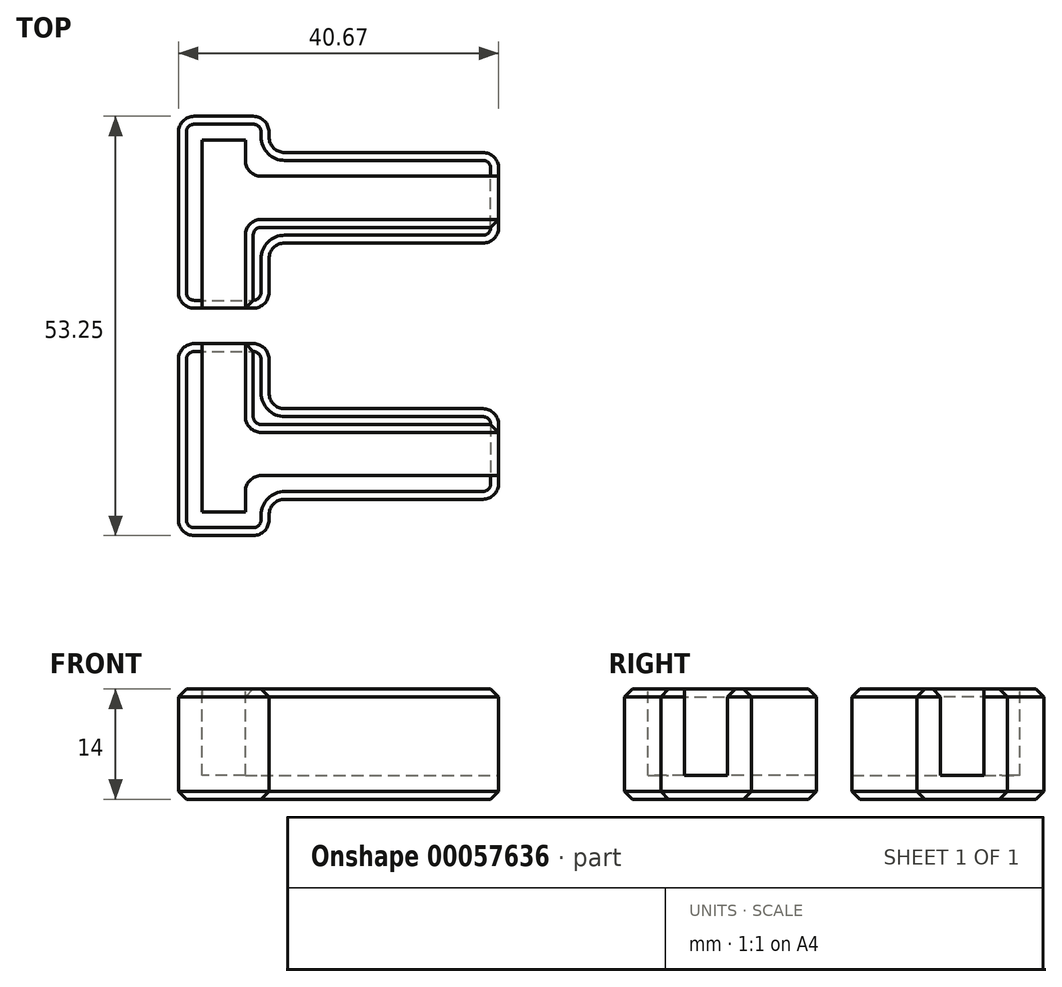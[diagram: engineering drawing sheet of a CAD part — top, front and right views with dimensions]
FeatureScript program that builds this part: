
annotation { "Feature Type Name" : "Feature", "Feature Type Description" : "" }
export const myFeature = defineFeature(function(context is Context, id is Id, definition is map)
    precondition{}
    {
        {
            var Q0;
            Q0=qCreatedBy(makeId("Top.planeOp"),FACE);
            var sketch = newSketch(context, id + "F0", { "sketchPlane" : qUnion([Q0])});
            skLineSegment(sketch, "E0", {"start": v(-6.24, -15.63) * mm, "end": v(22.93, -15.63) * mm});
            skLineSegment(sketch, "E1", {"start": v(22.93, -15.63) * mm, "end": v(22.93, -4.13) * mm});
            skLineSegment(sketch, "E2", {"start": v(22.93, -4.13) * mm, "end": v(-6.24, -4.13) * mm});
            skLineSegment(sketch, "E3", {"start": v(-6.24, -4.13) * mm, "end": v(-6.24, 4.14) * mm});
            skLineSegment(sketch, "E4", {"start": v(-6.24, 4.14) * mm, "end": v(-17.74, 4.14) * mm});
            skLineSegment(sketch, "E5", {"start": v(-17.74, 4.14) * mm, "end": v(-17.74, -20.23) * mm});
            skLineSegment(sketch, "E6", {"start": v(-17.74, -20.23) * mm, "end": v(-6.24, -20.23) * mm});
            skLineSegment(sketch, "E7", {"start": v(-6.24, -20.23) * mm, "end": v(-6.24, -15.63) * mm});
            skLineSegment(sketch, "E8", {"start": v(-14.74, 4.14) * mm, "end": v(-14.74, -17.23) * mm});
            skLineSegment(sketch, "E9", {"start": v(-14.74, -17.23) * mm, "end": v(-9.24, -17.23) * mm});
            skLineSegment(sketch, "E10", {"start": v(-9.24, -17.23) * mm, "end": v(-9.24, -12.63) * mm});
            skLineSegment(sketch, "E11", {"start": v(-9.24, -12.63) * mm, "end": v(22.93, -12.63) * mm});
            skLineSegment(sketch, "E12", {"start": v(-9.24, 4.14) * mm, "end": v(-9.24, -7.13) * mm});
            skLineSegment(sketch, "E13", {"start": v(-9.24, -7.13) * mm, "end": v(22.93, -7.13) * mm});
            skSolve(sketch);
        }
        {
            var Q0;
            Q0 = qSketchRegion(id + "F0", true);
            extrude(context, id + "F1", {"entities" : qUnion([Q0]), "oppositeDirection" : true, "depth" : 14 * mm});
        }
        {
            var Q0;
            {var subQ1=sQuery(id+"F0.wireOp",EDGE,"E8");Q0=makeQuery(id+"F0.imprint","IMPRINT",FACE,{"disambiguationData":[TD([[makeQuery(id+"F0.imprint","IMPRINT",EDGE,{"derivedFrom":subQ1}),1.0]])]});}
            extrude(context, id + "F2", {"entities" : qUnion([Q0]), "operationType" : NewBodyOperationType.REMOVE, "oppositeDirection" : true, "depth" : 11 * mm});
        }
        {
            var Q0;
            Q0=makeQuery(id+"F1.opExtrude","SWEPT_EDGE",EDGE,{"disambiguationData":[OSD([sQuery(id+"F0.wireOp",EDGE,"E6"),sQuery(id+"F0.wireOp",EDGE,"E7")])]});
            var Q1;
            Q1=makeQuery(id+"F1.opExtrude","SWEPT_EDGE",EDGE,{"disambiguationData":[OSD([sQuery(id+"F0.wireOp",EDGE,"E5"),sQuery(id+"F0.wireOp",EDGE,"E6")])]});
            var Q2;
            Q2=makeQuery(id+"F1.opExtrude","SWEPT_EDGE",EDGE,{"disambiguationData":[OSD([sQuery(id+"F0.wireOp",EDGE,"E0"),sQuery(id+"F0.wireOp",EDGE,"E7")])]});
            var Q3;
            Q3=makeQuery(id+"F1.opExtrude","SWEPT_EDGE",EDGE,{"disambiguationData":[OSD([sQuery(id+"F0.wireOp",EDGE,"E0"),sQuery(id+"F0.wireOp",EDGE,"E1")])]});
            var Q4;
            Q4=makeQuery(id+"F1.opExtrude","SWEPT_EDGE",EDGE,{"disambiguationData":[OSD([sQuery(id+"F0.wireOp",EDGE,"E4"),sQuery(id+"F0.wireOp",EDGE,"E5")])]});
            var Q5;
            Q5=makeQuery(id+"F1.opExtrude","SWEPT_EDGE",EDGE,{"disambiguationData":[OSD([sQuery(id+"F0.wireOp",EDGE,"E3"),sQuery(id+"F0.wireOp",EDGE,"E4")])]});
            var Q6;
            Q6=makeQuery(id+"F1.opExtrude","SWEPT_EDGE",EDGE,{"disambiguationData":[OSD([sQuery(id+"F0.wireOp",EDGE,"E1"),sQuery(id+"F0.wireOp",EDGE,"E2")])]});
            var Q7;
            Q7=makeQuery(id+"F1.opExtrude","SWEPT_EDGE",EDGE,{"disambiguationData":[OSD([sQuery(id+"F0.wireOp",EDGE,"E2"),sQuery(id+"F0.wireOp",EDGE,"E3")])]});
            var Q8;
            Q8=makeQuery(id+"F2.boolean.opBoolean","COPY",EDGE,{"derivedFrom":makeQuery(id+"F2.opExtrude","SWEPT_EDGE",EDGE,{"disambiguationData":[OSD([sQuery(id+"F0.wireOp",EDGE,"E10"),sQuery(id+"F0.wireOp",EDGE,"E11")])]})});
            var Q9;
            Q9=makeQuery(id+"F2.boolean.opBoolean","COPY",EDGE,{"derivedFrom":makeQuery(id+"F2.opExtrude","SWEPT_EDGE",EDGE,{"disambiguationData":[OSD([sQuery(id+"F0.wireOp",EDGE,"E12"),sQuery(id+"F0.wireOp",EDGE,"E13")])]})});
            fillet(context, id + "F3", {"entities" : qUnion([Q0, Q1, Q2, Q3, Q4, Q5, Q6, Q7, Q8, Q9]), "radius" : 2 * mm, "tangentPropagation" : true, "allowEdgeOverflow" : false});
        }
        {
            var Q0;
            Q0=makeQuery(id+"F2.boolean.opBoolean","COPY",EDGE,{"derivedFrom":makeQuery(id+"F2.opExtrude","CAP_EDGE",EDGE,{"disambiguationData":[OSD([sQuery(id+"F0.wireOp",EDGE,"E11")])],"isStart":true})});
            var Q1;
            Q1=makeQuery(id+"F2.boolean.opBoolean","COPY",EDGE,{"derivedFrom":makeQuery(id+"F2.opExtrude","CAP_EDGE",EDGE,{"disambiguationData":[OSD([sQuery(id+"F0.wireOp",EDGE,"E10")])],"isStart":true})});
            var Q2;
            Q2=makeQuery(id+"F2.boolean.opBoolean","COPY",EDGE,{"derivedFrom":makeQuery(id+"F2.opExtrude","CAP_EDGE",EDGE,{"disambiguationData":[OSD([sQuery(id+"F0.wireOp",EDGE,"E9")])],"isStart":true})});
            var Q3;
            Q3=makeQuery(id+"F2.boolean.opBoolean","COPY",EDGE,{"derivedFrom":makeQuery(id+"F2.opExtrude","CAP_EDGE",EDGE,{"disambiguationData":[OSD([sQuery(id+"F0.wireOp",EDGE,"E8")])],"isStart":true})});
            var Q4;
            Q4=makeQuery(id+"F2.boolean.opBoolean","COPY",EDGE,{"derivedFrom":makeQuery(id+"F2.opExtrude","CAP_EDGE",EDGE,{"disambiguationData":[OSD([sQuery(id+"F0.wireOp",EDGE,"E12")])],"isStart":true})});
            var Q5;
            Q5=makeQuery(id+"F2.boolean.opBoolean","COPY",EDGE,{"derivedFrom":makeQuery(id+"F2.opExtrude","CAP_EDGE",EDGE,{"disambiguationData":[OSD([sQuery(id+"F0.wireOp",EDGE,"E13")])],"isStart":true})});
            var Q6;
            Q6=makeQuery(id+"F1.opExtrude","CAP_EDGE",EDGE,{"disambiguationData":[OSD([sQuery(id+"F0.wireOp",EDGE,"E0")])],"isStart":true});
            var Q7;
            {var subQ0=sQuery(id+"F0.wireOp",EDGE,"E4");var subQ1=sQuery(id+"F0.wireOp",EDGE,"E3");var subQ2=sQuery(id+"F0.wireOp",EDGE,"E2");var subQ3=sQuery(id+"F0.wireOp",EDGE,"E1");Q7=makeQuery(id+"F3.opFillet","BLEND_EDGE",EDGE,{"blendedFrom":[makeQuery(id+"F1.opExtrude","SWEPT_EDGE",EDGE,{"disambiguationData":[OSD([subQ1,subQ0])]}),makeQuery(id+"F2.boolean.opBoolean","SPLIT",FACE,{"disambiguationData":[TD([makeQuery(id+"F1.opExtrude","SWEPT_FACE",FACE,{"disambiguationData":[OSD([subQ2])]})])],"derivedFrom":makeQuery(id+"F1.opExtrude","CAP_FACE",FACE,{"disambiguationData":[OSD([sQuery(id+"F0.wireOp",EDGE,"E0"),subQ3,subQ2,subQ1,subQ0,sQuery(id+"F0.wireOp",EDGE,"E5"),sQuery(id+"F0.wireOp",EDGE,"E6"),sQuery(id+"F0.wireOp",EDGE,"E7")])],"isStart":true})})],"blendedInto":[makeQuery(id+"F2.boolean.opBoolean","SPLIT",FACE,{"disambiguationData":[TD([makeQuery(id+"F1.opExtrude","SWEPT_FACE",FACE,{"disambiguationData":[OSD([subQ2])]})])],"derivedFrom":makeQuery(id+"F1.opExtrude","CAP_FACE",FACE,{"disambiguationData":[OSD([sQuery(id+"F0.wireOp",EDGE,"E0"),subQ3,subQ2,subQ1,subQ0,sQuery(id+"F0.wireOp",EDGE,"E5"),sQuery(id+"F0.wireOp",EDGE,"E6"),sQuery(id+"F0.wireOp",EDGE,"E7")])],"isStart":true})})]});}
            chamfer(context, id + "F4", {"entities" : qUnion([Q0, Q1, Q2, Q3, Q4, Q5, Q6, Q7]), "width" : 1 * mm, "tangentPropagation" : true});
        }
        {
            var Q0;
            Q0=makeQuery(id+"F1.opExtrude","CAP_FACE",FACE,{"disambiguationData":[OSD([sQuery(id+"F0.wireOp",EDGE,"E0"),sQuery(id+"F0.wireOp",EDGE,"E1"),sQuery(id+"F0.wireOp",EDGE,"E2"),sQuery(id+"F0.wireOp",EDGE,"E3"),sQuery(id+"F0.wireOp",EDGE,"E4"),sQuery(id+"F0.wireOp",EDGE,"E5"),sQuery(id+"F0.wireOp",EDGE,"E6"),sQuery(id+"F0.wireOp",EDGE,"E7")])],"isStart":false});
            chamfer(context, id + "F5", {"entities" : qUnion([Q0]), "width" : 1 * mm, "tangentPropagation" : true});
        }
        {
            var Q0;
            Q0=makeQuery(id+"F1.opExtrude","SWEPT_BODY",BODY,{"disambiguationData":[OSD([sQuery(id+"F0.wireOp",EDGE,"E0"),sQuery(id+"F0.wireOp",EDGE,"E1"),sQuery(id+"F0.wireOp",EDGE,"E2"),sQuery(id+"F0.wireOp",EDGE,"E3"),sQuery(id+"F0.wireOp",EDGE,"E4"),sQuery(id+"F0.wireOp",EDGE,"E5"),sQuery(id+"F0.wireOp",EDGE,"E6"),sQuery(id+"F0.wireOp",EDGE,"E7")])]});
            var Q1;
            Q1=makeQuery(id+"F1.opExtrude","SWEPT_FACE",FACE,{"disambiguationData":[OSD([sQuery(id+"F0.wireOp",EDGE,"E4")])]});
            mirror(context, id + "F6", {"entities" : qUnion([Q0]), "mirrorPlane" : qUnion([Q1])});
        }
        {
            var Q0;
            Q0=makeQuery(id+"F6.opPattern","COPY",BODY,{"derivedFrom":makeQuery(id+"F1.opExtrude","SWEPT_BODY",BODY,{"disambiguationData":[OSD([sQuery(id+"F0.wireOp",EDGE,"E0"),sQuery(id+"F0.wireOp",EDGE,"E1"),sQuery(id+"F0.wireOp",EDGE,"E2"),sQuery(id+"F0.wireOp",EDGE,"E3"),sQuery(id+"F0.wireOp",EDGE,"E4"),sQuery(id+"F0.wireOp",EDGE,"E5"),sQuery(id+"F0.wireOp",EDGE,"E6"),sQuery(id+"F0.wireOp",EDGE,"E7")])]}),"instanceName":"1"});
            transform(context, id + "F7", {"entities" : qUnion([Q0]), "transformType" : TransformType.TRANSLATION_3D, "dx" : 0 * mm, "dy" : 4.5 * mm, "dz" : 0 * mm, "makeCopy" : false});
        }
    });
